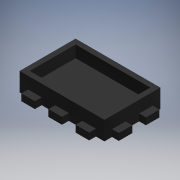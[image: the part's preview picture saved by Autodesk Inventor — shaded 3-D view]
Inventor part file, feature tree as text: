
AUTODESK INVENTOR PART (.ipt)
format: ipt  version: 2019 (Build 230136000, 136)  size: 198,144 bytes
history: native  units: mm
features: extrude x3, sketch x3, projected_geometry x2
ambient origin geometry x8: Origin, YZ Plane, XZ Plane, XY Plane, X Axis, Y Axis, Z Axis, Center Point
bodies: Solid1 (feature_tree)
feature tree (8):
  extrude  "Extrusion1"  Depth=41.0mm
  extrude  "Extrusion2"  Depth=4.0mm
  extrude  "Extrusion3"  Depth=7.0mm TaperAngle=0.0deg
  sketch  "Sketch1"  dims[d0=58.0mm d1=41.0mm]
  sketch  "Sketch2"  dims[d2=4.0mm d3=0.0mm d4=4.0mm]
  projected_geometry  "Projected Loop1"
  sketch  "Sketch3"  dims[d5=3.0mm d6=7.0mm d7=0.0mm d8=8.0mm d9=8.0mm d10=4.0mm d13=4.0mm d14=8.0mm d15=4.0mm d16=0.0mm]
  projected_geometry  "Projected Loop2"
